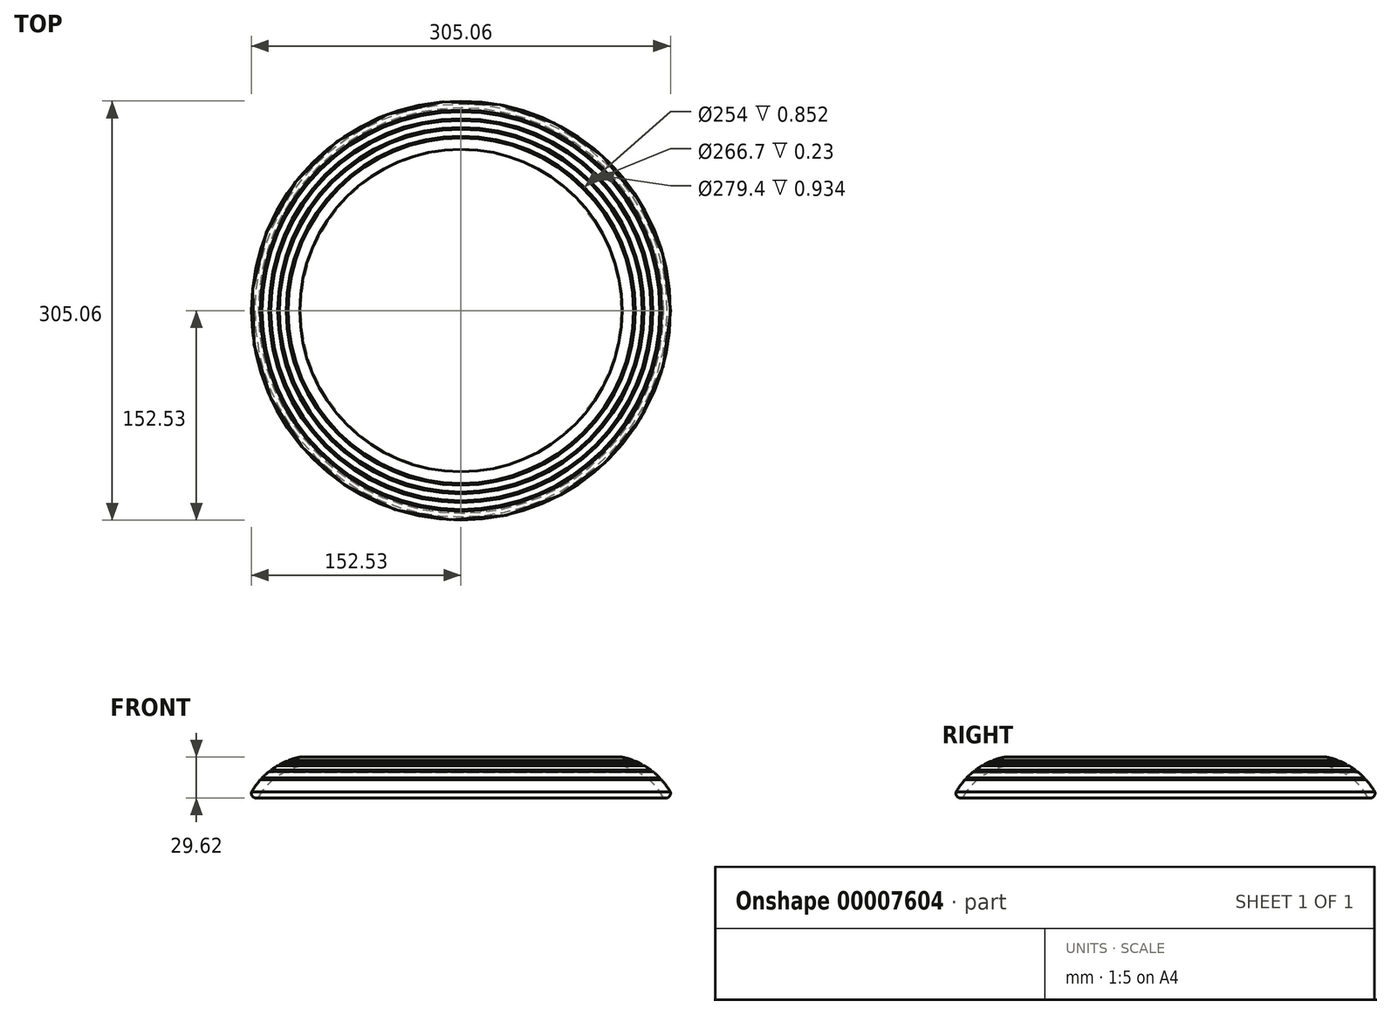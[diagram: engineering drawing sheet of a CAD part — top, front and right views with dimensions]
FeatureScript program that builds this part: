
annotation { "Feature Type Name" : "Feature", "Feature Type Description" : "" }
export const myFeature = defineFeature(function(context is Context, id is Id, definition is map)
    precondition{}
    {
        {
            var Q0;
            Q0=qCreatedBy(makeId("Front.planeOp"),FACE);
            var sketch = newSketch(context, id + "F0", { "sketchPlane" : qUnion([Q0])});
            skLineSegment(sketch, "E0", {"start": v(0, 1.78) * mm, "end": v(0, -23.62) * mm});
            skLineSegment(sketch, "E1", {"start": v(0, -23.62) * mm, "end": v(-152.4, -23.62) * mm});
            skLineSegment(sketch, "E2", {"start": v(-129.08, 1.78) * mm, "end": v(0, 1.78) * mm});
            skArc(sketch, "E3", {"start": v(-96.37, 1.78) * mm, "mid": v(-128.5, -1.83) * mm, "end": v(-152.4, -23.62) * mm});
            skArc(sketch, "E4", {"start": v(-152.4, -23.62) * mm, "mid": v(-152.11, -26.2) * mm, "end": v(-150.1, -27.84) * mm});
            skLineSegment(sketch, "E5", {"start": v(-150.1, -27.84) * mm, "end": v(0, -27.84) * mm});
            skLineSegment(sketch, "E6", {"start": v(0, -27.84) * mm, "end": v(0, -23.62) * mm});
            skSolve(sketch);
        }
        {
            var Q0;
            {var subQ5=sQuery(id+"F0.wireOp",EDGE,"E0");Q0=makeQuery(id+"F0.imprint","IMPRINT",FACE,{"disambiguationData":[TD([[makeQuery(id+"F0.imprint","IMPRINT",EDGE,{"derivedFrom":subQ5}),-1.0]])]});}
            var Q1;
            Q1=makeQuery(id+"F0.imprint","IMPRINT",FACE,{"disambiguationData":[TD([[makeQuery(id+"F0.imprint","IMPRINT",EDGE,{"derivedFrom":sQuery(id+"F0.wireOp",EDGE,"E1")}),1.0]])]});
            var Q2;
            Q2=sQuery(id+"F0.wireOp",EDGE,"E0");
            revolve(context, id + "F1", {"entities" : qUnion([Q0, Q1]), "axis" : qUnion([Q2]), "revolveType" : RevolveType.FULL});
        }
        {
            var Q0;
            Q0=makeQuery(id+"F1.opRevolve","SWEPT_FACE",FACE,{"disambiguationData":[OSD([sQuery(id+"F0.wireOp",EDGE,"E5")])]});
            shell(context, id + "F2", {"entities" : qUnion([Q0]), "thickness" : 6.35 * mm});
        }
        {
            var Q0;
            Q0=makeQuery(id+"F1.opRevolve","SWEPT_FACE",FACE,{"disambiguationData":[OSD([sQuery(id+"F0.wireOp",EDGE,"E2")])]});
            var sketch = newSketch(context, id + "F3", { "sketchPlane" : qUnion([Q0])});
            skCircle(sketch, "E7", {"center": v(0, 0) * mm, "radius": 146.05 * mm});
            skCircle(sketch, "E8", {"center": v(0, 0) * mm, "radius": 139.7 * mm});
            skCircle(sketch, "E9", {"center": v(0, 0) * mm, "radius": 133.35 * mm});
            skCircle(sketch, "E10", {"center": v(0, 0) * mm, "radius": 127 * mm});
            skCircle(sketch, "E11", {"center": v(0, 0) * mm, "radius": 144.78 * mm});
            skCircle(sketch, "E12", {"center": v(0, 0) * mm, "radius": 138.43 * mm});
            skCircle(sketch, "E13", {"center": v(0, 0) * mm, "radius": 132.08 * mm});
            skCircle(sketch, "E14", {"center": v(0, 0) * mm, "radius": 125.73 * mm});
            skSolve(sketch);
        }
        {
            var Q0;
            Q0=makeQuery(id+"F3.imprint","IMPRINT",FACE,{"disambiguationData":[TD([[makeQuery(id+"F3.imprint","IMPRINT",EDGE,{"derivedFrom":sQuery(id+"F3.wireOp",EDGE,"E10")}),1.0]])]});
            extrude(context, id + "F4", {"entities" : qUnion([Q0]), "operationType" : NewBodyOperationType.REMOVE, "oppositeDirection" : true, "depth" : 3.8 * mm});
        }
        {
            var Q0;
            Q0=makeQuery(id+"F3.imprint","IMPRINT",FACE,{"disambiguationData":[TD([[makeQuery(id+"F3.imprint","IMPRINT",EDGE,{"derivedFrom":sQuery(id+"F3.wireOp",EDGE,"E9")}),1.0]])]});
            extrude(context, id + "F5", {"entities" : qUnion([Q0]), "operationType" : NewBodyOperationType.REMOVE, "oppositeDirection" : true, "depth" : 6.35 * mm});
        }
        {
            var Q0;
            Q0=makeQuery(id+"F3.imprint","IMPRINT",FACE,{"disambiguationData":[TD([[makeQuery(id+"F3.imprint","IMPRINT",EDGE,{"derivedFrom":sQuery(id+"F3.wireOp",EDGE,"E8")}),1.0]])]});
            extrude(context, id + "F6", {"entities" : qUnion([Q0]), "operationType" : NewBodyOperationType.REMOVE, "oppositeDirection" : true, "depth" : 11.43 * mm});
        }
        {
            var Q0;
            Q0=makeQuery(id+"F3.imprint","IMPRINT",FACE,{"disambiguationData":[TD([[makeQuery(id+"F3.imprint","IMPRINT",EDGE,{"derivedFrom":sQuery(id+"F3.wireOp",EDGE,"E7")}),1.0]])]});
            extrude(context, id + "F7", {"entities" : qUnion([Q0]), "operationType" : NewBodyOperationType.REMOVE, "oppositeDirection" : true, "depth" : 16.5 * mm});
        }
    });
